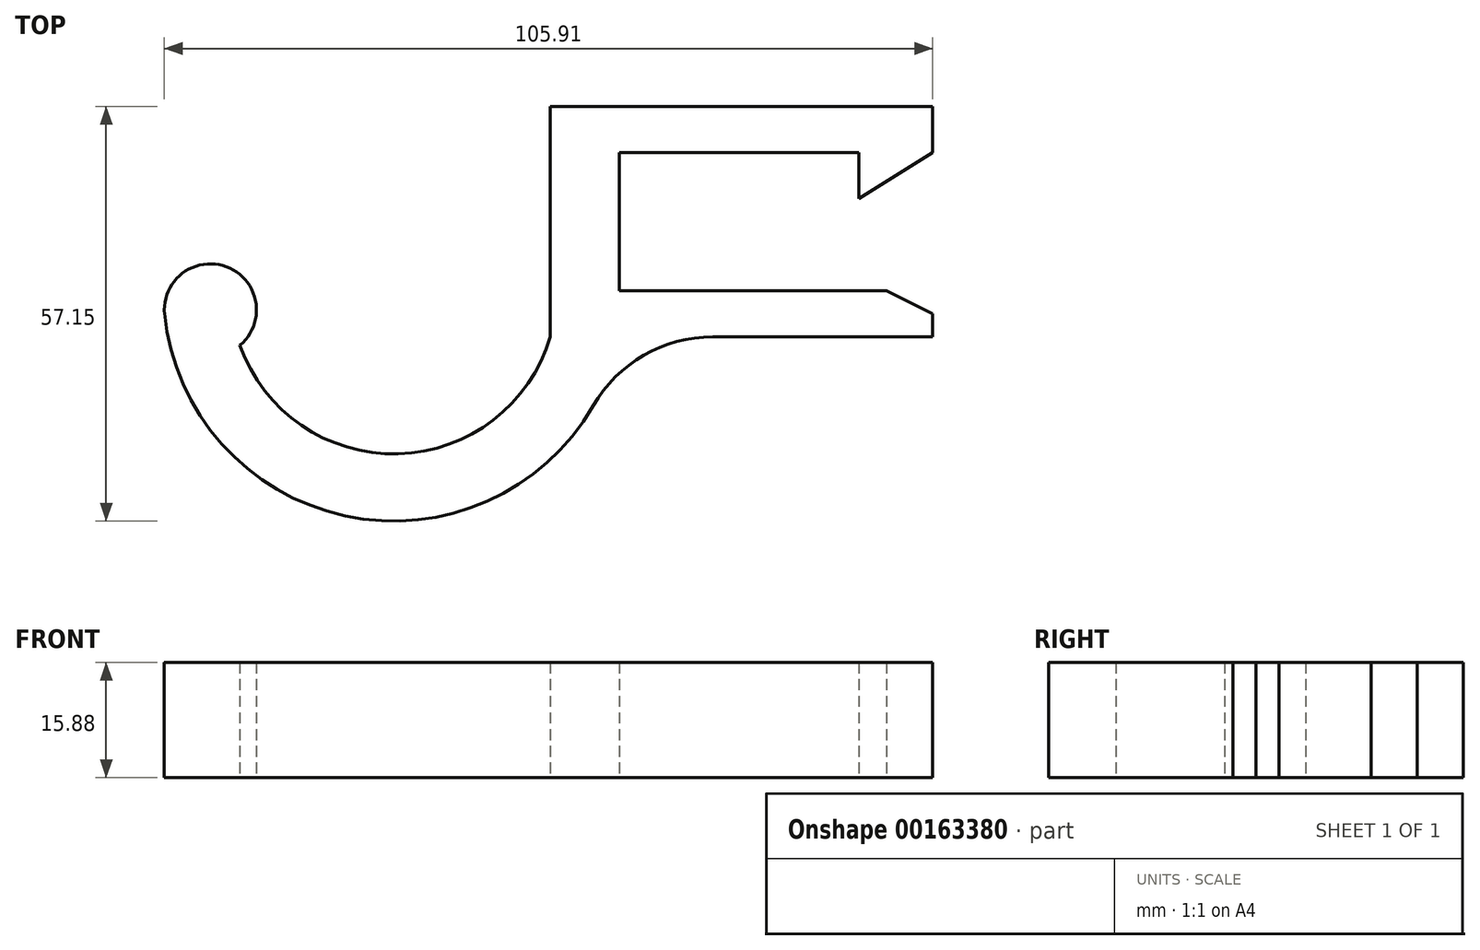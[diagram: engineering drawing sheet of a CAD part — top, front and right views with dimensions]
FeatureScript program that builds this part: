
annotation { "Feature Type Name" : "Feature", "Feature Type Description" : "" }
export const myFeature = defineFeature(function(context is Context, id is Id, definition is map)
    precondition{}
    {
        {
            var Q0;
            Q0=qCreatedBy(makeId("Top.planeOp"),FACE);
            var sketch = newSketch(context, id + "F2", { "sketchPlane" : qUnion([Q0])});
            skLineSegment(sketch, "E0.bottom", {"start": v(0, 0) * mm, "end": v(36.83, 0) * mm});
            skLineSegment(sketch, "E0.top", {"start": v(0, 19.05) * mm, "end": v(33.02, 19.05) * mm});
            skLineSegment(sketch, "E0.left", {"start": v(0, 0) * mm, "end": v(0, 19.05) * mm});
            skLineSegment(sketch, "E0.right", {"start": v(33.02, 12.7) * mm, "end": v(33.02, 19.05) * mm});
            skLineSegment(sketch, "E1.bottom", {"start": v(0, -6.35) * mm, "end": v(43.18, -6.35) * mm});
            skLineSegment(sketch, "E1.top", {"start": v(-9.53, 25.4) * mm, "end": v(43.18, 25.4) * mm});
            skLineSegment(sketch, "E1.left", {"start": v(-9.52, -6.35) * mm, "end": v(-9.53, 25.4) * mm});
            skLineSegment(sketch, "E1.right", {"start": v(43.18, -6.35) * mm, "end": v(43.18, -3.18) * mm});
            skLineSegment(sketch, "E2", {"start": v(33.02, 12.7) * mm, "end": v(43.18, 19.05) * mm});
            skLineSegment(sketch, "E3", {"start": v(43.18, 19.05) * mm, "end": v(43.18, 19.05) * mm});
            skLineSegment(sketch, "E4.trimOffspring", {"start": v(43.18, 19.05) * mm, "end": v(43.18, 25.4) * mm});
            skLineSegment(sketch, "E5", {"start": v(43.18, -3.18) * mm, "end": v(36.83, 0) * mm});
            skPoint(sketch, "E6.orphan", {"position": v(43.18, 0) * mm});
            skArc(sketch, "E7", {"start": v(-62.7, -3.1) * mm, "mid": v(-32.75, -31.7) * mm, "end": v(0, -6.35) * mm});
            skPoint(sketch, "E8", {"position": v(-9.53, 9.53) * mm});
            skPoint(sketch, "E9", {"position": v(0, -6.35) * mm});
            skArc(sketch, "E10", {"start": v(-62.73, -2.65) * mm, "mid": v(-62.72, -2.87) * mm, "end": v(-62.7, -3.1) * mm});
            skLineSegment(sketch, "E11", {"start": v(-9.53, 25.4) * mm, "end": v(-58.1, -2.65) * mm, "construction": true});
            skArc(sketch, "E12", {"start": v(-52.31, -7.52) * mm, "mid": v(-53.69, 3.1) * mm, "end": v(-62.73, -2.65) * mm});
            skArc(sketch, "E13.trimOffspring", {"start": v(-52.31, -7.52) * mm, "mid": v(-30.5, -22.49) * mm, "end": v(-9.52, -6.35) * mm});
            skSolve(sketch);
        }
        {
            var Q0;
            Q0=makeQuery(id+"F2.imprint","IMPRINT",FACE,{"disambiguationData":[TD([[makeQuery(id+"F2.imprint","IMPRINT",EDGE,{"derivedFrom":sQuery(id+"F2.wireOp",EDGE,"E0.bottom")}),-1.0]])]});
            extrude(context, id + "F0", {"entities" : qUnion([Q0]), "endBound" : BoundingType.SYMMETRIC, "depth" : 15.88 * mm});
        }
        {
            var Q0;
            Q0=makeQuery(id+"F0.opExtrude","SWEPT_EDGE",EDGE,{"disambiguationData":[OSD([sQuery(id+"F2.wireOp",EDGE,"E1.bottom"),sQuery(id+"F2.wireOp",EDGE,"E7")])]});
            fillet(context, id + "F1", {"entities" : qUnion([Q0]), "radius" : 19.05 * mm, "tangentPropagation" : true, "allowEdgeOverflow" : false});
        }
    });
